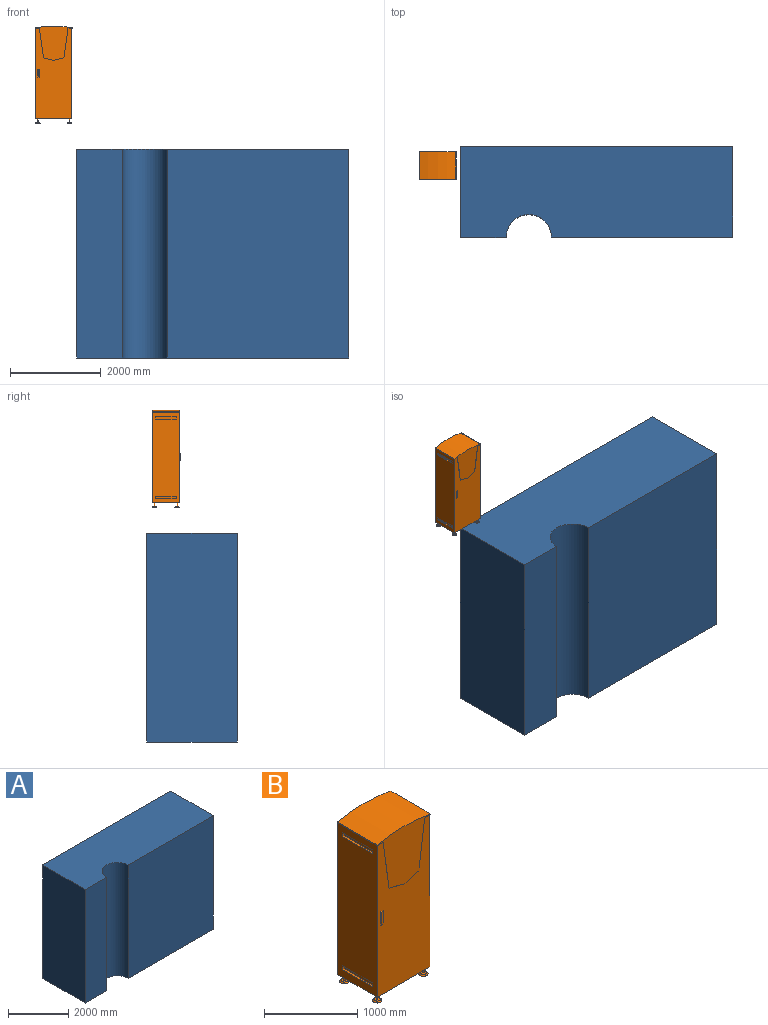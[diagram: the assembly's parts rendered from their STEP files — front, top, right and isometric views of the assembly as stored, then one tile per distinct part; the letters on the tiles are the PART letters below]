
ASSEMBLY  parts=2 mates=1
PART A: 8 faces, bbox 6000x2000x4600 mm
  f0: plane 4600x2000mm, normal (-1,0,0), area 9200000mm2, adj f1,f5,f6,f7
  f1: plane 4600x1000mm, normal (0,-1,0), area 4600000mm2, adj f0,f2,f6,f7
  f2: cylinder r=500mm len=4600mm, axis (0,0,1), area 7225663.1mm2, adj f1,f3,f6,f7
  f3: plane 4600x4000mm, normal (0,-1,0), area 18400000mm2, adj f2,f4,f6,f7
  f4: plane 4600x2000mm, normal (1,0,0), area 9200000mm2, adj f3,f5,f6,f7
  f5: plane 6000x4600mm, normal (0,1,0), area 27600000mm2, adj f0,f4,f6,f7
  f6: plane 6000x2000mm, normal (0,0,-1), area 11607300.9mm2, adj f0,f1,f2,f3,f4,f5
  f7: plane 6000x2000mm, normal (0,0,1), area 11607300.9mm2, adj f0,f1,f2,f3,f4,f5
PART B: 56 faces, bbox 815x615x2140 mm
  f0: plane 2000x800mm, normal (0,-1,0), area 1228500mm2, adj f1,f2,f3,f41,f42,f43,f44,f46
  f1: plane 2000x600mm, normal (1,0,0), area 1155000mm2, adj f0,f3,f4,f15,f16,f17,f18,f20
  f2: plane 2000x600mm, normal (-1,0,0), area 1155000mm2, adj f0,f3,f4,f5,f6,f7,f8,f10
  f3: plane 800x600mm, normal (0,0,-1), area 479293.1mm2, adj f0,f1,f2,f4,f25,f26,f27,f28
  f4: plane 2050x815mm, normal (0,1,0), area 1629400.7mm2, adj f1,f2,f3,f51,f52,f53,f54,f55
  f5: plane 50x25mm, normal (0,-1,0), area 1250mm2, adj f2,f6,f8,f9
  f6: plane 450x25mm, normal (0,0,1), area 11250mm2, adj f2,f5,f7,f9
  f7: plane 50x25mm, normal (0,1,0), area 1250mm2, adj f2,f6,f8,f9
  f8: plane 450x25mm, normal (0,0,-1), area 11250mm2, adj f2,f5,f7,f9
  f9: plane 450x50mm, normal (-1,0,0), area 22500mm2, adj f5,f6,f7,f8
  f10: plane 50x25mm, normal (0,-1,0), area 1250mm2, adj f2,f11,f13,f14
  f11: plane 450x25mm, normal (0,0,1), area 11250mm2, adj f2,f10,f12,f14
  f12: plane 50x25mm, normal (0,1,0), area 1250mm2, adj f2,f11,f13,f14
  f13: plane 450x25mm, normal (0,0,-1), area 11250mm2, adj f2,f10,f12,f14
  f14: plane 450x50mm, normal (-1,0,0), area 22500mm2, adj f10,f11,f12,f13
  f15: plane 450x25mm, normal (0,0,-1), area 11250mm2, adj f1,f16,f18,f19
  f16: plane 50x25mm, normal (0,1,0), area 1250mm2, adj f1,f15,f17,f19
  f17: plane 450x25mm, normal (0,0,1), area 11250mm2, adj f1,f16,f18,f19
  f18: plane 50x25mm, normal (0,-1,0), area 1250mm2, adj f1,f15,f17,f19
  f19: plane 450x50mm, normal (1,0,0), area 22500mm2, adj f15,f16,f17,f18
  f20: plane 450x25mm, normal (0,0,-1), area 11250mm2, adj f1,f21,f23,f24
  f21: plane 50x25mm, normal (0,1,0), area 1250mm2, adj f1,f20,f22,f24
  f22: plane 450x25mm, normal (0,0,1), area 11250mm2, adj f1,f21,f23,f24
  f23: plane 50x25mm, normal (0,-1,0), area 1250mm2, adj f1,f20,f22,f24
  f24: plane 450x50mm, normal (1,0,0), area 22500mm2, adj f20,f21,f22,f23
  f25: cylinder r=7.5mm len=75mm, axis (0,0,1), area 3534.3mm2, adj f3,f31
  f26: cylinder r=7.5mm len=75mm, axis (0,0,1), area 3534.3mm2, adj f3,f34
  f27: cylinder r=7.5mm len=75mm, axis (0,0,1), area 3534.3mm2, adj f3,f40
  f28: cylinder r=7.5mm len=75mm, axis (0,0,1), area 3534.3mm2, adj f3,f37
  f29: cone r=35mm half-angle=45deg, axis (0,0,-1), area 5664.7mm2, adj f30,f31
  f30: plane 100x100mm, normal (0,0,-1), area 7854mm2, adj f29
  f31: plane 70x70mm, normal (0,0,1), area 3671.7mm2, adj f25,f29
  f32: cone r=35mm half-angle=45deg, axis (0,0,-1), area 5664.7mm2, adj f33,f34
  f33: plane 100x100mm, normal (0,0,-1), area 7854mm2, adj f32
  f34: plane 70x70mm, normal (0,0,1), area 3671.7mm2, adj f26,f32
  f35: cone r=35mm half-angle=45deg, axis (0,0,-1), area 5664.7mm2, adj f36,f37
  f36: plane 100x100mm, normal (0,0,-1), area 7854mm2, adj f35
  f37: plane 70x70mm, normal (0,0,1), area 3671.7mm2, adj f28,f35
  f38: cone r=35mm half-angle=45deg, axis (0,0,-1), area 5664.7mm2, adj f39,f40
  f39: plane 100x100mm, normal (0,0,-1), area 7854mm2, adj f38
  f40: plane 70x70mm, normal (0,0,1), area 3671.7mm2, adj f27,f38
  f41: plane 650x90mm, normal (-0.99,0,-0.14), area 3281mm2, adj f0,f42,f45,f51
  f42: plane 225x60mm, normal (-0.26,0,-0.97), area 1164.3mm2, adj f0,f41,f43,f45
  f43: plane 225x60mm, normal (0.26,0,-0.97), area 1164.3mm2, adj f0,f42,f44,f45
  f44: plane 650x90mm, normal (0.99,0,-0.14), area 3281mm2, adj f0,f43,f45,f52
  f45: plane 815x760mm, normal (0,-1,0), area 393900.7mm2, adj f41,f42,f43,f44,f51,f52,f53,f54
  f46: plane 40x15mm, normal (0,-0.26,0.97), area 558.8mm2, adj f0,f47,f49,f50
  f47: plane 175x15mm, normal (-0.97,-0.26,0), area 2655.2mm2, adj f0,f46,f48,f50
  f48: plane 40x15mm, normal (0,-0.26,-0.97), area 558.8mm2, adj f0,f47,f49,f50
  f49: plane 175x15mm, normal (0.97,-0.26,0), area 2655.2mm2, adj f0,f46,f48,f50
  f50: plane 166.96x31.96mm, normal (0,-1,0), area 5336.3mm2, adj f46,f47,f48,f49
  f51: plane 605x92.5mm, normal (0,0,-1), area 4962.5mm2, adj f0,f2,f4,f41,f45,f54
  f52: plane 605x92.5mm, normal (0,0,-1), area 4962.5mm2, adj f0,f1,f4,f44,f45,f53
  f53: plane 605x8.05mm, normal (1,0,0), area 4867.8mm2, adj f4,f45,f52,f55
  f54: plane 605x8.05mm, normal (-1,0,0), area 4867.8mm2, adj f4,f45,f51,f55
  f55: cylinder r=2000mm len=815mm, axis (0,1,0), area 496551.9mm2, adj f4,f45,f53,f54
PLACE A t=(-2084.94,2278.98,2646.24)mm
PLACE B t=(-4031.78,3554.89,4319.94)mm
MATE parallel B.f27 <-> A.f7  axis (0,0,-1) through (-4443.09,4104.89,3229.12)mm
